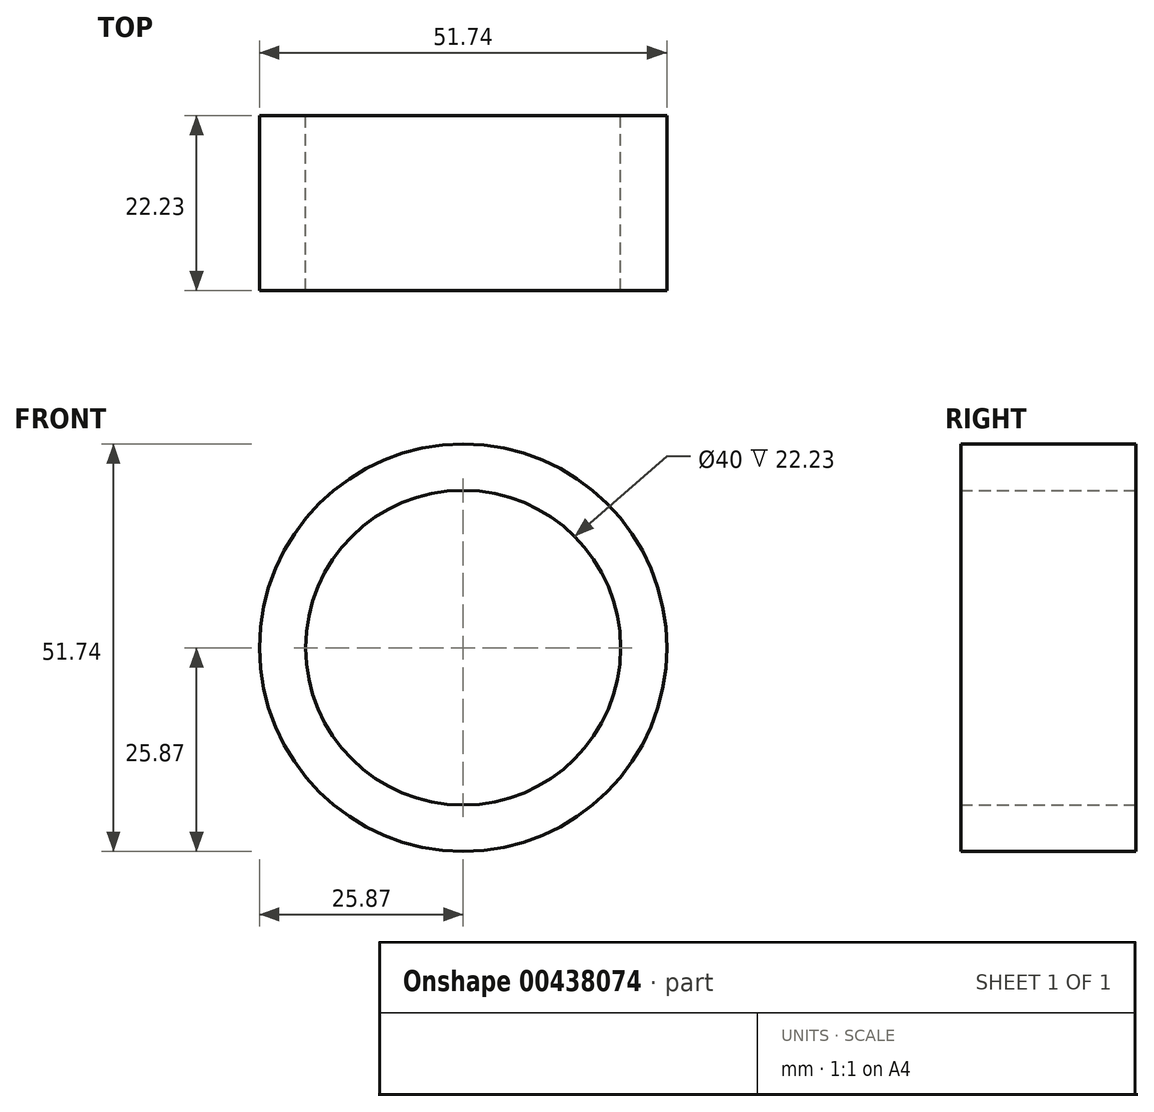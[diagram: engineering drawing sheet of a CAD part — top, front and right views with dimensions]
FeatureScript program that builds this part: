
annotation { "Feature Type Name" : "Feature", "Feature Type Description" : "" }
export const myFeature = defineFeature(function(context is Context, id is Id, definition is map)
    precondition{}
    {
        {
            var Q0;
            Q0=qCreatedBy(makeId("Front.planeOp"),FACE);
            var sketch = newSketch(context, id + "F0", { "sketchPlane" : qUnion([Q0])});
            skCircle(sketch, "E0", {"center": v(0, 0) * mm, "radius": 25.87 * mm});
            skSolve(sketch);
        }
        {
            var Q0;
            Q0 = qSketchRegion(id + "F0", true);
            extrude(context, id + "F1", {"entities" : qUnion([Q0]), "depth" : 22.23 * mm});
        }
        {
            var Q0;
            Q0=qCreatedBy(makeId("Front.planeOp"),FACE);
            var sketch = newSketch(context, id + "F2", { "sketchPlane" : qUnion([Q0])});
            skPoint(sketch, "E1", {"position": v(0, 0) * mm});
            skSolve(sketch);
        }
        {
            var Q0;
            Q0=sQuery(id+"F2.wireOp",VERTEX,"E1");
            var Q1;
            Q1=makeQuery(id+"F1.opExtrude","SWEPT_BODY",BODY,{"disambiguationData":[OSD([sQuery(id+"F0.wireOp",EDGE,"E0")])]});
            hole(context, id + "F3", {"style" : HoleStyle.SIMPLE, "endStyle" : HoleEndStyle.THROUGH, "oppositeDirection" : true, "holeDiameter" : 40 * mm, "isTappedThrough" : true, "tappedDepth" : 12 * mm, "tapClearance" : 3, "locations" : qUnion([Q0]), "scope" : qUnion([Q1])});
        }
    });
